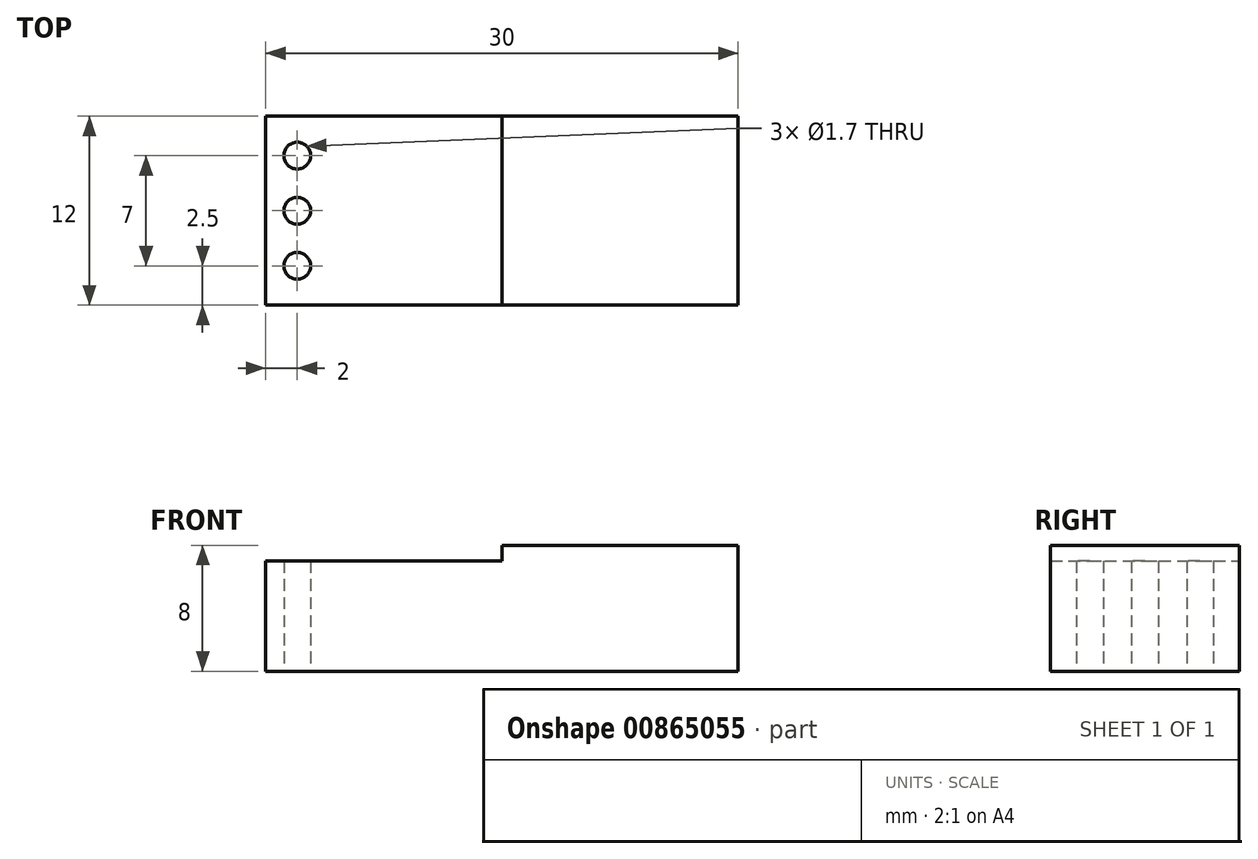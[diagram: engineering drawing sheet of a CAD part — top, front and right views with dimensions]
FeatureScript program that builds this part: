
annotation { "Feature Type Name" : "Feature", "Feature Type Description" : "" }
export const myFeature = defineFeature(function(context is Context, id is Id, definition is map)
    precondition{}
    {
        {
            var Q0;
            Q0=qCreatedBy(makeId("Top.planeOp"),FACE);
            var sketch = newSketch(context, id + "F0", { "sketchPlane" : qUnion([Q0])});
            skLineSegment(sketch, "E0.bottom", {"start": v(15, -6) * mm, "end": v(-15, -6) * mm});
            skLineSegment(sketch, "E0.top", {"start": v(15, 6) * mm, "end": v(-15, 6) * mm});
            skLineSegment(sketch, "E0.left", {"start": v(15, -6) * mm, "end": v(15, 6) * mm});
            skLineSegment(sketch, "E0.right", {"start": v(-15, -6) * mm, "end": v(-15, 6) * mm});
            skPoint(sketch, "E0.middle", {"position": v(0, 0) * mm});
            skSolve(sketch);
        }
        {
            var Q0;
            Q0 = qSketchRegion(id + "F0", true);
            extrude(context, id + "F1", {"entities" : qUnion([Q0]), "endBound" : BoundingType.SYMMETRIC, "depth" : 8 * mm, "offsetDistance" : 25 * mm});
        }
        {
            var Q0;
            Q0=makeQuery(id+"F1.opExtrude","SWEPT_FACE",FACE,{"disambiguationData":[OSD([sQuery(id+"F0.wireOp",EDGE,"E0.top")])]});
            var sketch = newSketch(context, id + "F2", { "sketchPlane" : qUnion([Q0])});
            skPoint(sketch, "E1.oppositeSnap0", {"position": v(0, 4) * mm});
            skLineSegment(sketch, "E1.bottom", {"start": v(15, 4) * mm, "end": v(0, 4) * mm});
            skLineSegment(sketch, "E1.top", {"start": v(15, 3) * mm, "end": v(0, 3) * mm});
            skLineSegment(sketch, "E1.left", {"start": v(15, 4) * mm, "end": v(15, 3) * mm});
            skLineSegment(sketch, "E1.right", {"start": v(0, 4) * mm, "end": v(0, 3) * mm});
            skSolve(sketch);
        }
        {
            var Q0;
            Q0 = qSketchRegion(id + "F2", true);
            extrude(context, id + "F3", {"entities" : qUnion([Q0]), "operationType" : NewBodyOperationType.REMOVE, "oppositeDirection" : true, "depth" : 25 * mm, "offsetDistance" : 25 * mm});
        }
        {
            var Q0;
            Q0=makeQuery(id+"F1.opExtrude","CAP_FACE",FACE,{"disambiguationData":[OSD([sQuery(id+"F0.wireOp",EDGE,"E0.bottom"),sQuery(id+"F0.wireOp",EDGE,"E0.top"),sQuery(id+"F0.wireOp",EDGE,"E0.left"),sQuery(id+"F0.wireOp",EDGE,"E0.right")])],"isStart":true});
            var sketch = newSketch(context, id + "F4", { "sketchPlane" : qUnion([Q0])});
            skPoint(sketch, "E2", {"position": v(-13, -3.5) * mm});
            skLineSegment(sketch, "E3", {"start": v(0, 0) * mm, "end": v(-13.82, 0) * mm, "construction": true});
            skLineSegment(sketch, "E4", {"start": v(-13, -3.5) * mm, "end": v(-13, 0) * mm, "construction": true});
            skPoint(sketch, "E5", {"position": v(-13, 0) * mm});
            skPoint(sketch, "E6.MirrorP", {"position": v(-13, 3.5) * mm});
            skSolve(sketch);
        }
        {
            var Q0;
            Q0=sQuery(id+"F4.wireOp",VERTEX,"E2");
            var Q1;
            Q1=sQuery(id+"F4.wireOp",VERTEX,"E5");
            var Q2;
            Q2=sQuery(id+"F4.wireOp",VERTEX,"E6.MirrorP");
            var Q3;
            Q3=makeQuery(id+"F1.opExtrude","SWEPT_BODY",BODY,{"disambiguationData":[OSD([sQuery(id+"F0.wireOp",EDGE,"E0.bottom"),sQuery(id+"F0.wireOp",EDGE,"E0.top"),sQuery(id+"F0.wireOp",EDGE,"E0.left"),sQuery(id+"F0.wireOp",EDGE,"E0.right")])]});
            hole(context, id + "F5", {"style" : HoleStyle.SIMPLE, "endStyle" : HoleEndStyle.THROUGH, "holeDiameter" : 1.7 * mm, "majorDiameter" : 5 * mm, "isTappedThrough" : true, "tappedDepth" : 3.5 * mm, "tapClearance" : 3, "locations" : qUnion([Q0, Q1, Q2]), "scope" : qUnion([Q3])});
        }
    });
